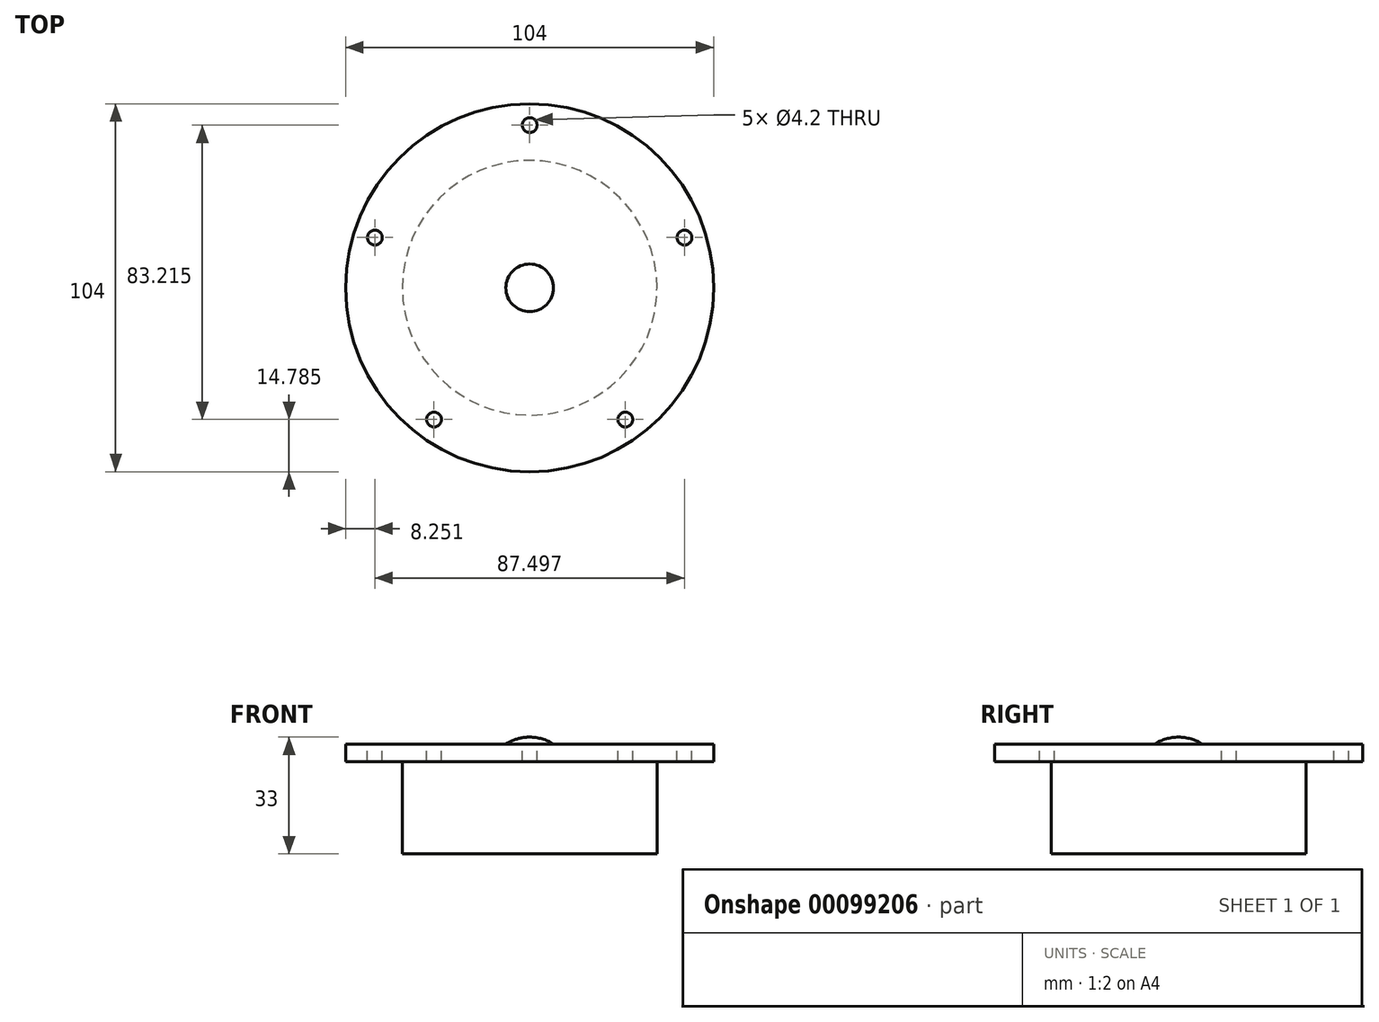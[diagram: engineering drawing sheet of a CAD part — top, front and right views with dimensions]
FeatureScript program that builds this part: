
annotation { "Feature Type Name" : "Feature", "Feature Type Description" : "" }
export const myFeature = defineFeature(function(context is Context, id is Id, definition is map)
    precondition{}
    {
        {
            var Q0;
            Q0=qCreatedBy(makeId("Front.planeOp"),FACE);
            var sketch = newSketch(context, id + "F0", { "sketchPlane" : qUnion([Q0])});
            skLineSegment(sketch, "E0", {"start": v(0, 0) * mm, "end": v(0, -23) * mm, "construction": true});
            skLineSegment(sketch, "E1", {"start": v(0, 0) * mm, "end": v(0, 33) * mm});
            skLineSegment(sketch, "E2", {"start": v(0, 0) * mm, "end": v(-36, 0) * mm});
            skLineSegment(sketch, "E3", {"start": v(-36, 0) * mm, "end": v(-36, 26.07) * mm});
            skLineSegment(sketch, "E4", {"start": v(-36, 26.07) * mm, "end": v(-52, 26.07) * mm});
            skLineSegment(sketch, "E5", {"start": v(-52, 26.07) * mm, "end": v(-52, 31.07) * mm});
            skLineSegment(sketch, "E6", {"start": v(-52, 31.07) * mm, "end": v(-6.73, 31.07) * mm});
            skArc(sketch, "E7", {"start": v(0, 33) * mm, "mid": v(-3.5, 32.5) * mm, "end": v(-6.73, 31.07) * mm});
            skSolve(sketch);
        }
        {
            var Q0;
            Q0=makeQuery(id+"F0.imprint","IMPRINT",FACE,{"disambiguationData":[TD([[makeQuery(id+"F0.imprint","IMPRINT",EDGE,{"derivedFrom":sQuery(id+"F0.wireOp",EDGE,"E1")}),1.0]])]});
            var Q1;
            Q1=sQuery(id+"F0.wireOp",EDGE,"E0");
            revolve(context, id + "F1", {"entities" : qUnion([Q0]), "axis" : qUnion([Q1]), "revolveType" : RevolveType.FULL});
        }
        {
            var Q0;
            Q0=makeQuery(id+"F1.opRevolve","SWEPT_FACE",FACE,{"disambiguationData":[OSD([sQuery(id+"F0.wireOp",EDGE,"E6")])]});
            var sketch = newSketch(context, id + "F2", { "sketchPlane" : qUnion([Q0])});
            skCircle(sketch, "E8.cCircle", {"center": v(0, 0) * mm, "radius": 46 * mm, "construction": true});
            skLineSegment(sketch, "E8.0", {"start": v(0, 46) * mm, "end": v(43.75, 14.21) * mm, "construction": true});
            skLineSegment(sketch, "E8.1", {"start": v(43.75, 14.21) * mm, "end": v(27.04, -37.21) * mm, "construction": true});
            skLineSegment(sketch, "E8.2", {"start": v(27.04, -37.21) * mm, "end": v(-27.04, -37.21) * mm, "construction": true});
            skLineSegment(sketch, "E8.3", {"start": v(-27.04, -37.21) * mm, "end": v(-43.75, 14.21) * mm, "construction": true});
            skLineSegment(sketch, "E8.4", {"start": v(-43.75, 14.21) * mm, "end": v(0, 46) * mm, "construction": true});
            skCircle(sketch, "E9", {"center": v(0, 46) * mm, "radius": 2.1 * mm});
            skCircle(sketch, "E10", {"center": v(43.75, 14.21) * mm, "radius": 2.1 * mm});
            skCircle(sketch, "E11", {"center": v(27.04, -37.21) * mm, "radius": 2.1 * mm});
            skCircle(sketch, "E12", {"center": v(-27.04, -37.21) * mm, "radius": 2.1 * mm});
            skCircle(sketch, "E13", {"center": v(-43.75, 14.21) * mm, "radius": 2.1 * mm});
            skSolve(sketch);
        }
        {
            var Q0;
            Q0 = qSketchRegion(id + "F2", true);
            extrude(context, id + "F3", {"entities" : qUnion([Q0]), "operationType" : NewBodyOperationType.REMOVE, "endBound" : BoundingType.UP_TO_NEXT, "oppositeDirection" : true, "depth" : 25.4 * mm});
        }
    });
